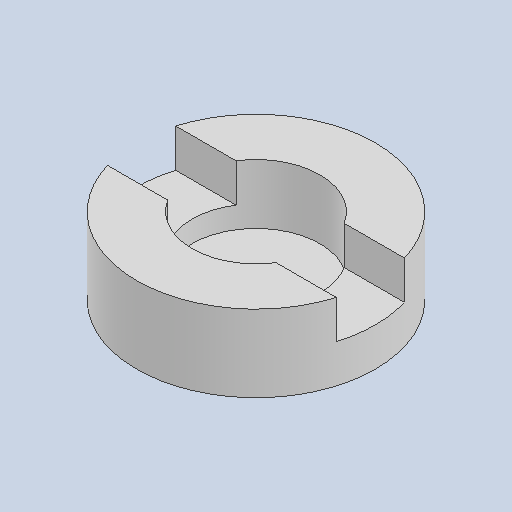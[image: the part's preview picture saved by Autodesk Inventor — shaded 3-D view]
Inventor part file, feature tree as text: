
AUTODESK INVENTOR PART (.ipt)
format: ipt  version: 2022.1 (Build 261234020, 234B)  size: 123,392 bytes
history: native  units: mm
features: sketch x4, extrude x4, hole x1
ambient origin geometry x8: Origin, YZ Plane, XZ Plane, XY Plane, X Axis, Y Axis, Z Axis, Center Point
bodies: Solid1 (feature_tree)
feature tree (9):
  sketch  "Sketch1"  dims[d0=28.0mm d1=15.0mm]
  extrude  "Extrusion1"  Depth=15.0mm
  extrude  "Extrusion2"  Depth=7.0mm
  extrude  "Extrusion3"  Depth=8.0mm TaperAngle=0.0deg
  hole  "Hole2"  [1 undecoded]
  extrude  "Extrusion4"  Depth=2.5mm TaperAngle=0.0deg
  sketch  "Sketch2"  dims[d2=7.0mm d3=0.0mm d4=28.0mm]
  sketch  "Sketch3"  dims[d5=8.0mm d6=8.0mm d7=0.0mm]
  sketch  "Sketch5"  dims[d8=2.0mm d9=0.0mm d17=28.0mm d18=4.5mm d19=6.0mm d20=10.59mm d21=3.0mm d22=90.0deg d23=8.0mm d24=20.594885mm d25=2.5mm d26=0.0mm]
note: 1 required parameter value undecoded (feature->parameter linkage not recoverable at this tier; creation-order binding heuristic only, values carry confidence <= 0.55)
